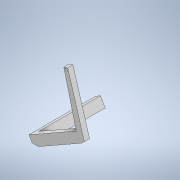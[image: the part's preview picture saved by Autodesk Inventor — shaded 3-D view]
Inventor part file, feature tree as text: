
AUTODESK INVENTOR PART (.ipt)
format: ipt  version: 2020 (Build 240168000, 168)  size: 142,848 bytes
history: native  units: mm
features: extrude x3, sketch x3
ambient origin geometry x8: Origin, YZ Plane, XZ Plane, XY Plane, X Axis, Y Axis, Z Axis, Center Point
bodies: Solid1 (feature_tree)
feature tree (6):
  extrude  "Extrusion1"  Depth=5.165078mm
  extrude  "Extrusion2"  Depth=120.895449mm
  extrude  "Extrusion3"  Depth=274.0mm
  sketch  "Sketch1"  dims[d1=10.542886mm d2=5.165078mm]
  sketch  "Sketch2"  dims[d10=233.093698mm d11=120.895449mm]
  sketch  "Sketch3"  dims[d12=24.243525mm d13=13.768721mm d14=196.983667mm d15=220.055283mm d16=159.179802mm d17=152.002472mm d18=356.005789mm d19=23.0mm d20=0.0mm d21=274.0mm d22=0.0mm d23=63.016mm d24=0.693mm d25=274.0mm d26=0.0mm]
